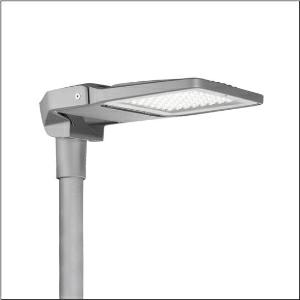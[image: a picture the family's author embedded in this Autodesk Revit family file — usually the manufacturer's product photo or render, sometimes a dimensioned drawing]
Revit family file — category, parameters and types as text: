
# Revit family: floodlight_fl_20_mini___pl61_5xa7672b2c4ac_d80c
name_source: partatom
category: Lighting Fixtures
units: mm (PartAtom-declared; Revit-internal decimal feet)

## family parameters
Cut with Voids When Loaded = No
Host = Face
Light Source = No
Part Type = Normal
Room Calculation Point = No
Round Connector Dimension = Use Diameter
Shared = No

## types (1)
- --- (1 x LED 4000K / CRI = 70 (unbekannt), 6350 lm, 4000K)
    Apparent Load = 51 VA
    CIE Flux Codes = 33 65 98 100 100
    Color Rendering = 70
    Color Temperature = 4000K
    Default Elevation = 1800 mm
    Description = Floodlight FL 20 mini, floodlight, primary light control with lens, of plastic, primary optical cover: protective disc, of toughened safety glass, transparent, light distribution: PL61, light emission: direct distribution, primary light characteristic: asymmetric, installation type: side-entry, post-top, LED, High Power LED, rated luminous flux: 6.350lm, luminous efficacy: 125lm/W, light colour: 740, colour temperature: 4000K, control gear: ECG Plus, control: flexible luminous flux parameterisation, time-dependent luminous flux control, digital communication interface, overheat protection, power reduction, electronic power reduction, with terminal, 5-pole, max. 2.5mm², mains connection: 220..240V, AC, 50/60Hz, rated input power: 51W, LED unit, of diecast aluminium, powder-coated, Siteco® metallic grey (DB 702S), corrosivity category C5 mid according to DIN EN ISO 12944, incl. 1x M20 cable gland for cable Ø 6.5..12mm, inclination adjustable: 0°, 5°, 10°, 15°, please order mast flange separately, length: 565mm, width: 335mm, height: 119mm, housing frame, of diecast aluminium, powder-coated, Siteco® metallic grey (DB 702S), mast flange adapter, of diecast aluminium, powder-coated, Siteco® metallic grey (DB 702S), DALI, protection rating (complete): IP66, insulation class (complete): insulation class II (safety insulation), certification: CE, ENEC, VDE, protection symbol: D, permissible operating ambient temperature: -40..+40°C, permissible operating ambient temperature for outdoor applications: -40..+50°C, standard: DIN EN 12944, packaging unit: 1 piece

Light Distribution: PL61
    Height = 62 mm  [stored 0.203412 ft]
    Lamp = 1 x LED 4000K / CRI >= 70 (unbekannt)
    Lamp Light Flux = 6350 lm
    Lamp count = 1
    Length = 565 mm
    Luminous efficacy = 125 lm/W
    Manufacturer = Siteco
    ModVariant = No
    Model = 5XA7672B2C4AC
    Number of Poles = 1
    OnlyDefault = Yes
    Power Factor = 1
    Product Name = Floodlight FL 20 mini | PL61
    Product group = floodlight | pylon top
    ProductGroupID = 6101
    Protection Class = Protection class II
    Protection Degree = IP 66
    RLX_Detail_Level = 1
    RLX_Emergency_Light_Flux = 0 lm
    RLX_Emergency_Type = 0
    RLX_Emergency_Type_DB = No
    RlxData = <blob elided: 102077 chars, md5=ea30ea91>
    Socket = socket
    Standby Power = 0 W
    System Light Flux = 6350 lm
    System Power = 51 W
    Type Comments = factory setting: luminous flux: 100 % | dim-lin: 254 | 520 mA
    Type Image = l_1005946.jpg
    URL = http://relux.com
    VarID = @adj_163233
    Voltage = 0 V
    Weight = 0.00 kg
    Width = 335 mm

note: [stored X ft] marks values corroborated as IEEE doubles in the binary element streams (Revit-internal decimal feet)

## geometry (parser evidence)
native form markers: Blend x4, Sweep x12
no freeform markers — native parametric forms only
